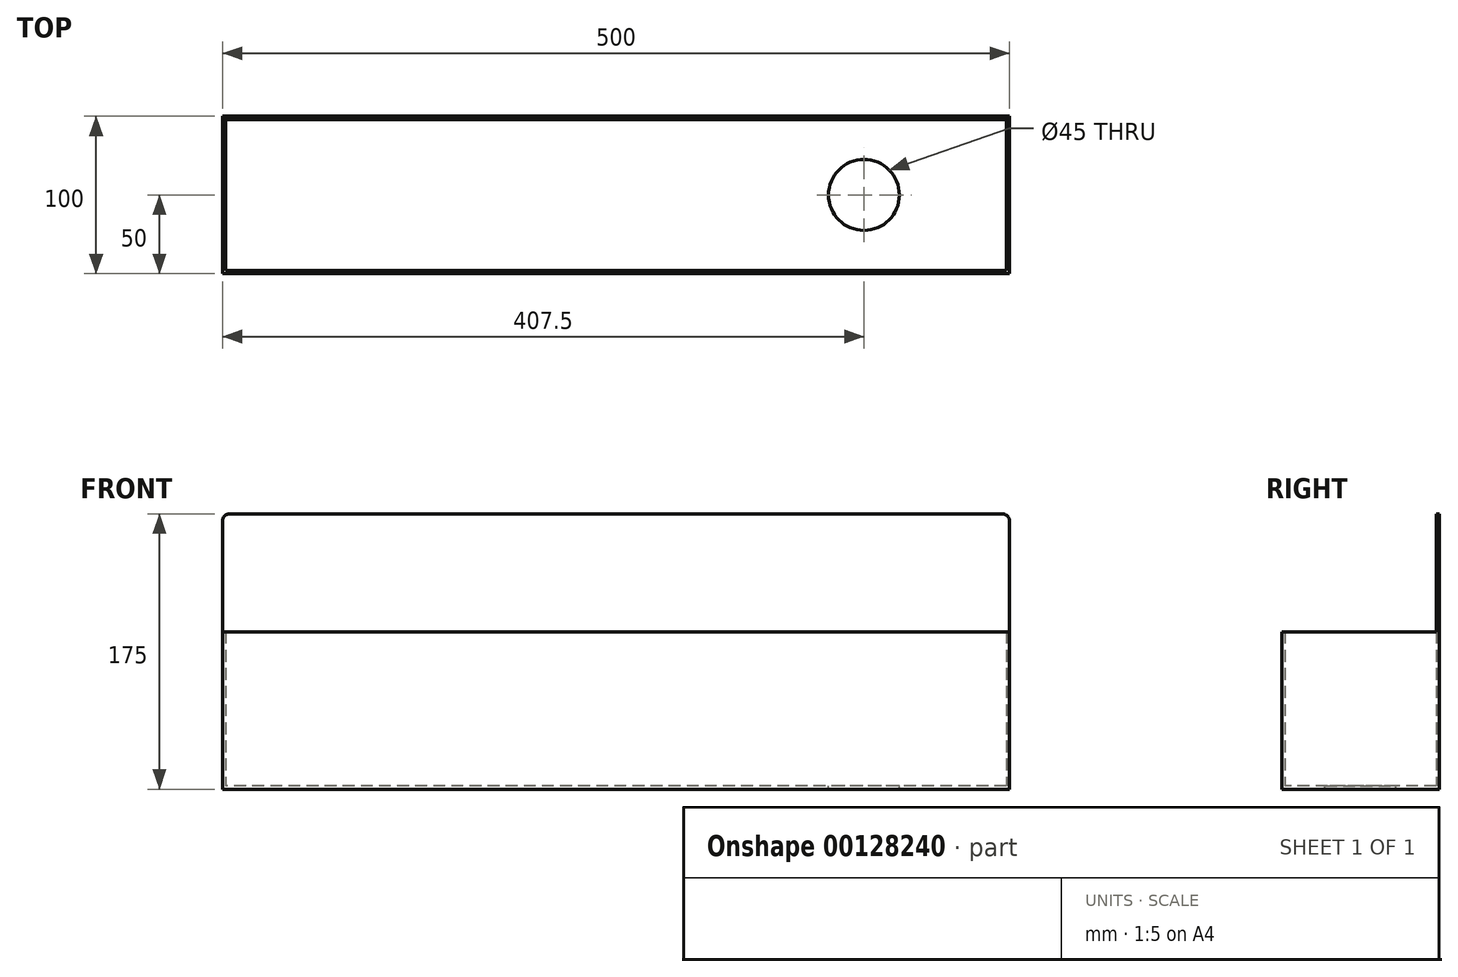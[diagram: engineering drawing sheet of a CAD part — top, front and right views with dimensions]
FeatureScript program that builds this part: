
annotation { "Feature Type Name" : "Feature", "Feature Type Description" : "" }
export const myFeature = defineFeature(function(context is Context, id is Id, definition is map)
    precondition{}
    {
        {
            var Q0;
            Q0=qCreatedBy(makeId("Right.planeOp"),FACE);
            var sketch = newSketch(context, id + "F0", { "sketchPlane" : qUnion([Q0])});
            skLineSegment(sketch, "E0.bottom", {"start": v(50, 50) * mm, "end": v(-50, 50) * mm});
            skLineSegment(sketch, "E0.top", {"start": v(50, -50) * mm, "end": v(-50, -50) * mm});
            skLineSegment(sketch, "E0.left", {"start": v(50, 50) * mm, "end": v(50, -50) * mm});
            skLineSegment(sketch, "E0.right", {"start": v(-50, 50) * mm, "end": v(-50, -50) * mm});
            skPoint(sketch, "E0.middle", {"position": v(0, 0) * mm});
            skSolve(sketch);
        }
        {
            var Q0;
            Q0 = qSketchRegion(id + "F0", true);
            extrude(context, id + "F1", {"entities" : qUnion([Q0]), "depth" : 500 * mm});
        }
        {
            var Q0;
            Q0=makeQuery(id+"F1.opExtrude","SWEPT_FACE",FACE,{"disambiguationData":[OSD([sQuery(id+"F0.wireOp",EDGE,"E0.bottom")])]});
            shell(context, id + "F2", {"entities" : qUnion([Q0]), "thickness" : 2 * mm});
        }
        {
            var Q0;
            Q0=makeQuery(id+"F1.opExtrude","SWEPT_FACE",FACE,{"disambiguationData":[OSD([sQuery(id+"F0.wireOp",EDGE,"E0.bottom")])]});
            var sketch = newSketch(context, id + "F3", { "sketchPlane" : qUnion([Q0])});
            skLineSegment(sketch, "E1.bottom", {"start": v(0, 50) * mm, "end": v(500, 50) * mm});
            skLineSegment(sketch, "E1.top", {"start": v(0, 48) * mm, "end": v(500, 48) * mm});
            skLineSegment(sketch, "E1.left", {"start": v(0, 50) * mm, "end": v(0, 48) * mm});
            skLineSegment(sketch, "E1.right", {"start": v(500, 50) * mm, "end": v(500, 48) * mm});
            skSolve(sketch);
        }
        {
            var Q0;
            Q0 = qSketchRegion(id + "F3", true);
            extrude(context, id + "F4", {"entities" : qUnion([Q0]), "operationType" : NewBodyOperationType.ADD, "depth" : 75 * mm});
        }
        {
            var Q0;
            Q0=makeQuery(id+"F4.opExtrude","CAP_EDGE",EDGE,{"disambiguationData":[OSD([sQuery(id+"F3.wireOp",EDGE,"E1.right")])],"isStart":false});
            var Q1;
            Q1=makeQuery(id+"F4.opExtrude","CAP_EDGE",EDGE,{"disambiguationData":[OSD([sQuery(id+"F3.wireOp",EDGE,"E1.left")])],"isStart":false});
            fillet(context, id + "F5", {"entities" : qUnion([Q0, Q1]), "radius" : 5 * mm, "tangentPropagation" : true, "allowEdgeOverflow" : false});
        }
        {
            var Q0;
            Q0=makeQuery(id+"F2.opShell","OFFSET_FACE",FACE,{"disambiguationData":[OSD([sQuery(id+"F0.wireOp",EDGE,"E0.top")])]});
            var sketch = newSketch(context, id + "F6", { "sketchPlane" : qUnion([Q0])});
            skCircle(sketch, "E2", {"center": v(407.5, 0) * mm, "radius": 22.5 * mm});
            skSolve(sketch);
        }
        {
            var Q0;
            Q0 = qSketchRegion(id + "F6", true);
            extrude(context, id + "F7", {"entities" : qUnion([Q0]), "operationType" : NewBodyOperationType.REMOVE, "endBound" : BoundingType.THROUGH_ALL, "oppositeDirection" : true, "depth" : 25 * mm});
        }
    });
